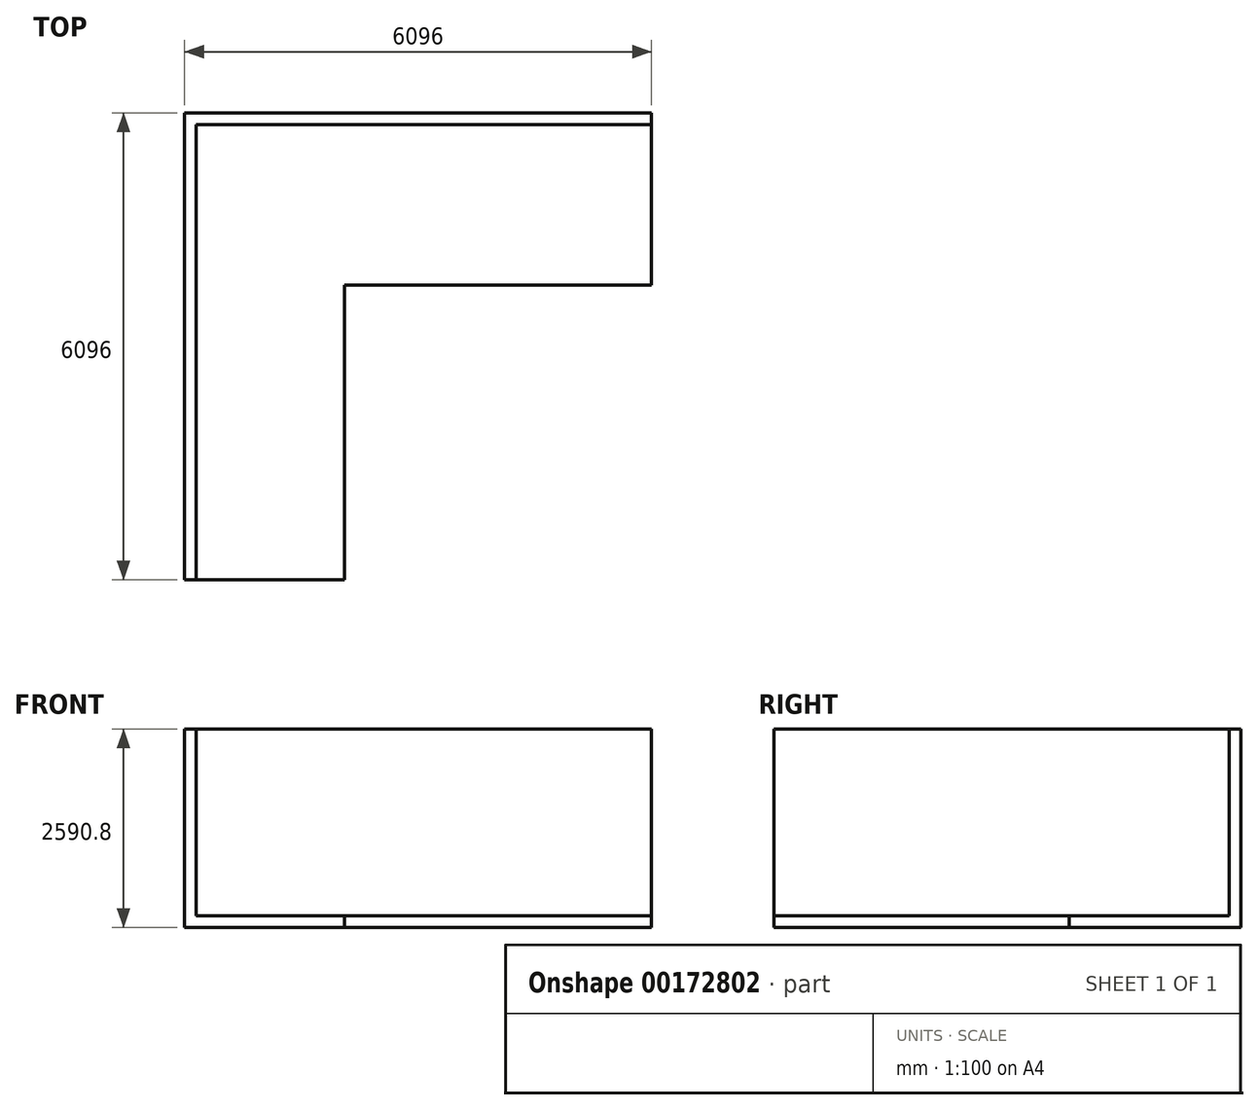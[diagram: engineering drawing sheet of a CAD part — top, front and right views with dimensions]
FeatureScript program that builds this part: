
annotation { "Feature Type Name" : "Feature", "Feature Type Description" : "" }
export const myFeature = defineFeature(function(context is Context, id is Id, definition is map)
    precondition{}
    {
        {
            var Q0;
            Q0=qCreatedBy(makeId("Top.planeOp"),FACE);
            var sketch = newSketch(context, id + "F0", { "sketchPlane" : qUnion([Q0])});
            skLineSegment(sketch, "E0.bottom", {"start": v(-2811.6, 3006.17) * mm, "end": v(3284.4, 3006.17) * mm});
            skLineSegment(sketch, "E0.top", {"start": v(-2811.6, -3089.83) * mm, "end": v(3284.4, -3089.83) * mm});
            skLineSegment(sketch, "E0.left", {"start": v(-2811.6, 3006.17) * mm, "end": v(-2811.6, -3089.83) * mm});
            skLineSegment(sketch, "E0.right", {"start": v(3284.4, 3006.17) * mm, "end": v(3284.4, -3089.83) * mm});
            skLineSegment(sketch, "E1.bottom", {"start": v(3284.4, -3089.83) * mm, "end": v(-728.3, -3089.83) * mm});
            skLineSegment(sketch, "E1.top", {"start": v(3284.4, 760.45) * mm, "end": v(-728.3, 760.45) * mm});
            skLineSegment(sketch, "E1.left", {"start": v(3284.4, -3089.83) * mm, "end": v(3284.4, 760.45) * mm});
            skLineSegment(sketch, "E1.right", {"start": v(-728.3, -3089.83) * mm, "end": v(-728.3, 760.45) * mm});
            skSolve(sketch);
        }
        {
            var Q0;
            Q0=makeQuery(id+"F0.imprint","IMPRINT",FACE,{"disambiguationData":[TD([[makeQuery(id+"F0.imprint","IMPRINT",EDGE,{"derivedFrom":sQuery(id+"F0.wireOp",EDGE,"E0.bottom")}),-1.0]])]});
            var Q1;
            Q1=makeQuery(id+"F0.imprint","IMPRINT",FACE,{"disambiguationData":[TD([[makeQuery(id+"F0.imprint","IMPRINT",EDGE,{"derivedFrom":sQuery(id+"F0.wireOp",EDGE,"E1.bottom")}),-1.0]])]});
            extrude(context, id + "F1", {"entities" : qUnion([Q0, Q1]), "depth" : 152.4 * mm, "offsetDistance" : 25.4 * mm});
        }
        {
            var Q0;
            Q0=makeQuery(id+"F1.opExtrude","CAP_FACE",FACE,{"disambiguationData":[OSD([sQuery(id+"F0.wireOp",EDGE,"E0.bottom"),sQuery(id+"F0.wireOp",EDGE,"E0.top"),sQuery(id+"F0.wireOp",EDGE,"E0.left"),sQuery(id+"F0.wireOp",EDGE,"E0.right"),sQuery(id+"F0.wireOp",EDGE,"E1.bottom"),sQuery(id+"F0.wireOp",EDGE,"E1.left")])],"isStart":false});
            var sketch = newSketch(context, id + "F2", { "sketchPlane" : qUnion([Q0])});
            skLineSegment(sketch, "E2.bottom", {"start": v(3284.4, -3089.83) * mm, "end": v(-2659.2, -3089.83) * mm});
            skLineSegment(sketch, "E2.top", {"start": v(3284.4, 2853.77) * mm, "end": v(-2659.2, 2853.77) * mm});
            skLineSegment(sketch, "E2.left", {"start": v(3284.4, -3089.83) * mm, "end": v(3284.4, 2853.77) * mm});
            skLineSegment(sketch, "E2.right", {"start": v(-2659.2, -3089.83) * mm, "end": v(-2659.2, 2853.77) * mm});
            skSolve(sketch);
        }
        {
            var Q0;
            {var subQ4=sQuery(id+"F2.wireOp",EDGE,"E2.top");Q0=makeQuery(id+"F2.imprint","IMPRINT",FACE,{"disambiguationData":[TD([[makeQuery(id+"F2.imprint","IMPRINT",EDGE,{"derivedFrom":subQ4}),-1.0]])]});}
            extrude(context, id + "F3", {"entities" : qUnion([Q0]), "operationType" : NewBodyOperationType.ADD, "depth" : 2438.4 * mm, "offsetDistance" : 25.4 * mm});
        }
    });
